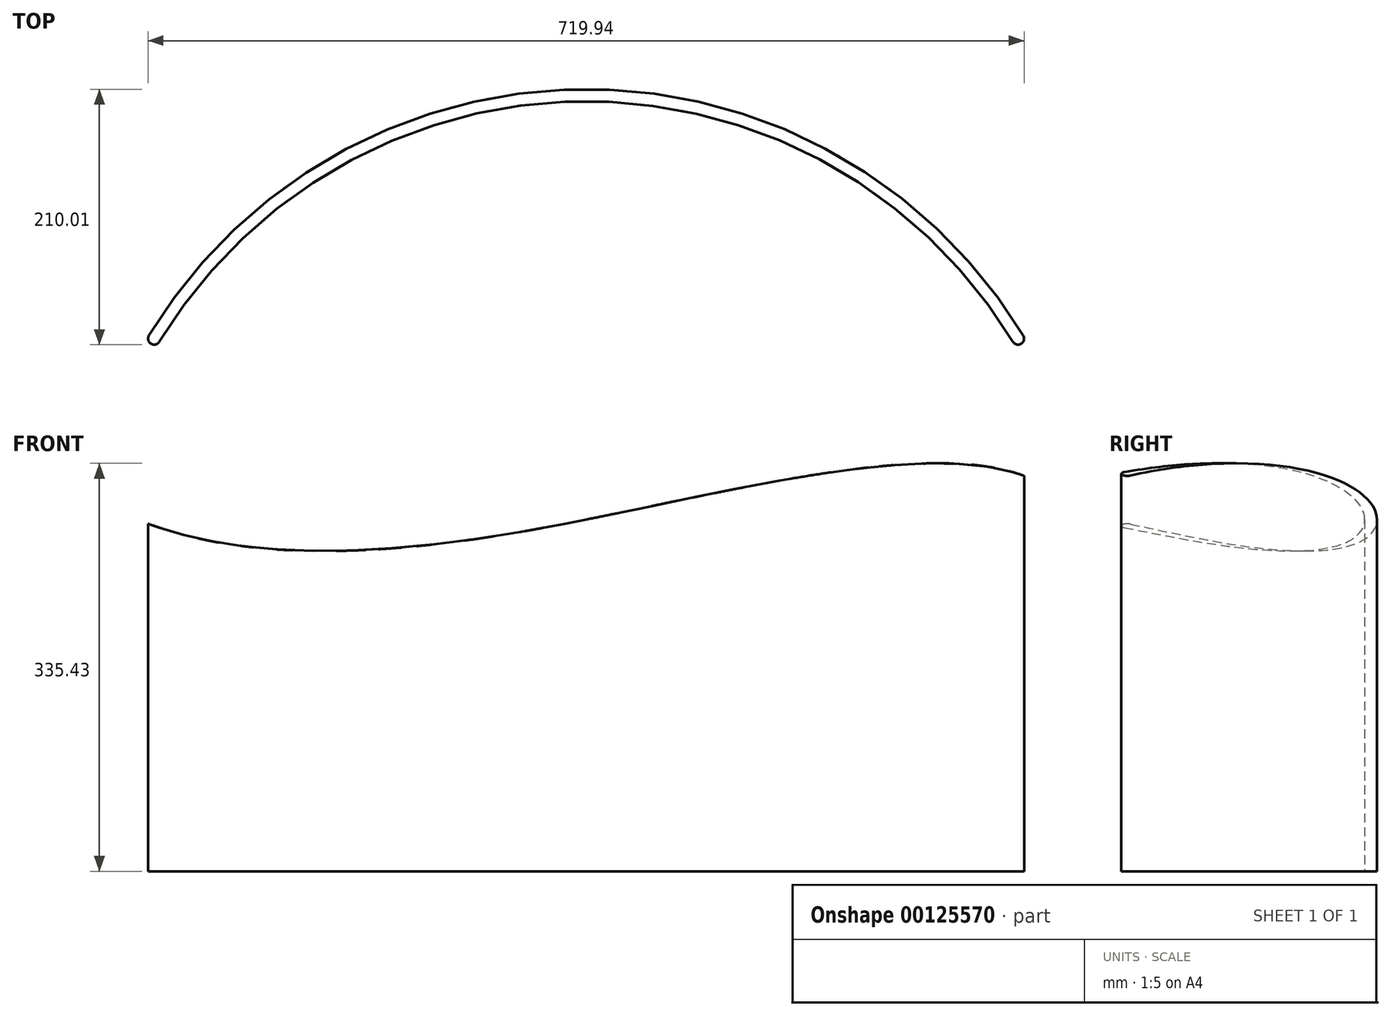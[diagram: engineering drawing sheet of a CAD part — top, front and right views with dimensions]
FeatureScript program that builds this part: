
annotation { "Feature Type Name" : "Feature", "Feature Type Description" : "" }
export const myFeature = defineFeature(function(context is Context, id is Id, definition is map)
    precondition{}
    {
        {
            var Q0;
            Q0=qCreatedBy(makeId("Top.planeOp"),FACE);
            var sketch = newSketch(context, id + "F0", { "sketchPlane" : qUnion([Q0])});
            skArc(sketch, "E0", {"start": v(352.14, 209.99) * mm, "mid": v(0, 410) * mm, "end": v(-352.14, 209.99) * mm});
            skArc(sketch, "E1.0", {"start": v(363.74, 209.99) * mm, "mid": v(0, 420) * mm, "end": v(-363.74, 209.99) * mm});
            skLineSegment(sketch, "E2", {"start": v(-363.74, 209.99) * mm, "end": v(-352.14, 209.99) * mm});
            skLineSegment(sketch, "E3", {"start": v(352.14, 209.99) * mm, "end": v(363.74, 209.99) * mm});
            skSolve(sketch);
        }
        {
            var Q0;
            Q0 = qSketchRegion(id + "F0", true);
            extrude(context, id + "F1", {"entities" : qUnion([Q0]), "depth" : 350 * mm});
        }
        {
            var Q0;
            Q0=makeQuery(id+"F1.opExtrude","SWEPT_EDGE",EDGE,{"disambiguationData":[OSD([sQuery(id+"F0.wireOp",EDGE,"E0"),sQuery(id+"F0.wireOp",EDGE,"E2")])]});
            var Q1;
            Q1=makeQuery(id+"F1.opExtrude","SWEPT_EDGE",EDGE,{"disambiguationData":[OSD([sQuery(id+"F0.wireOp",EDGE,"E1.0"),sQuery(id+"F0.wireOp",EDGE,"E2")])]});
            var Q2;
            Q2=makeQuery(id+"F1.opExtrude","SWEPT_EDGE",EDGE,{"disambiguationData":[OSD([sQuery(id+"F0.wireOp",EDGE,"E0"),sQuery(id+"F0.wireOp",EDGE,"E3")])]});
            var Q3;
            Q3=makeQuery(id+"F1.opExtrude","SWEPT_EDGE",EDGE,{"disambiguationData":[OSD([sQuery(id+"F0.wireOp",EDGE,"E1.0"),sQuery(id+"F0.wireOp",EDGE,"E3")])]});
            fillet(context, id + "F2", {"entities" : qUnion([Q0, Q1, Q2, Q3]), "radius" : 5 * mm, "tangentPropagation" : true, "allowEdgeOverflow" : false});
        }
        {
            var Q0;
            Q0=qCreatedBy(makeId("Front.planeOp"),FACE);
            cPlane(context, id + "F3", {"entities" : qUnion([Q0]), "cplaneType" : CPlaneType.OFFSET, "offset" : 25 * mm, "width" : 150 * mm, "height" : 150 * mm});
        }
        {
            var Q0;
            Q0=qCreatedBy(id+"F3.planeOp",FACE);
            var sketch = newSketch(context, id + "F4", { "sketchPlane" : qUnion([Q0])});
            skFitSpline(sketch, "E4", {"points": [v(-435.19, 317.41) * mm, v(-333.02, 277.2) * mm, v(-54.02, 278.96) * mm, v(363.14, 323.79) * mm, v(423.47, 266.24) * mm, v(428.93, 256) * mm], "startDerivative": vector(385.52, -153.38) * mm, "endDerivative": vector(233.63, -436.11) * mm});
            skLineSegment(sketch, "E5", {"start": v(-435.19, 317.41) * mm, "end": v(-435.19, 462.97) * mm});
            skLineSegment(sketch, "E6", {"start": v(-435.19, 462.97) * mm, "end": v(416.81, 462.97) * mm});
            skLineSegment(sketch, "E7", {"start": v(416.81, 462.97) * mm, "end": v(422.75, 267.6) * mm});
            skSolve(sketch);
        }
        {
            var Q0;
            Q0=makeQuery(id+"F4.imprint","IMPRINT",FACE,{"disambiguationData":[TD([[makeQuery(id+"F4.imprint","IMPRINT",EDGE,{"derivedFrom":sQuery(id+"F4.wireOp",EDGE,"E4")}),1.0]])]});
            extrude(context, id + "F5", {"entities" : qUnion([Q0]), "operationType" : NewBodyOperationType.REMOVE, "endBound" : BoundingType.THROUGH_ALL, "oppositeDirection" : true, "depth" : 25 * mm});
        }
    });
